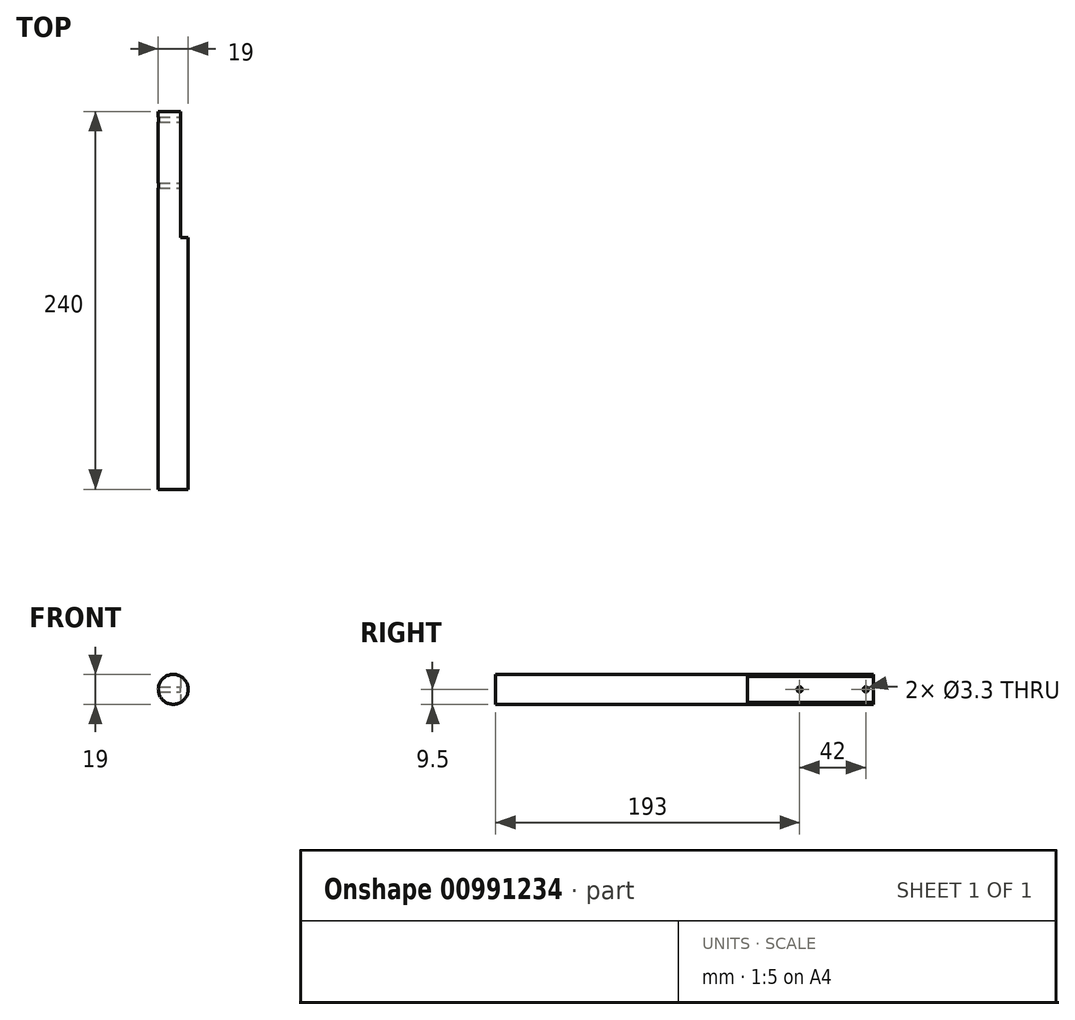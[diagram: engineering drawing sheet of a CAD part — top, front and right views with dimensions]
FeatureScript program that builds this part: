
annotation { "Feature Type Name" : "Feature", "Feature Type Description" : "" }
export const myFeature = defineFeature(function(context is Context, id is Id, definition is map)
    precondition{}
    {
        {
            var Q0;
            Q0=qCreatedBy(makeId("Front.planeOp"),FACE);
            var sketch = newSketch(context, id + "F0", { "sketchPlane" : qUnion([Q0])});
            skCircle(sketch, "E0", {"center": v(0, 0) * mm, "radius": 9.5 * mm});
            skSolve(sketch);
        }
        {
            var Q0;
            Q0 = qSketchRegion(id + "F0", true);
            extrude(context, id + "F1", {"entities" : qUnion([Q0]), "depth" : 240 * mm, "offsetDistance" : 25 * mm});
        }
        {
            var Q0;
            Q0=qCreatedBy(makeId("Right.planeOp"),FACE);
            cPlane(context, id + "F2", {"entities" : qUnion([Q0]), "cplaneType" : CPlaneType.OFFSET, "offset" : 9.5 * mm, "width" : 150 * mm, "height" : 150 * mm});
        }
        {
            var Q0;
            Q0=qCreatedBy(id+"F2.planeOp",FACE);
            var sketch = newSketch(context, id + "F3", { "sketchPlane" : qUnion([Q0])});
            skLineSegment(sketch, "E1.bottom", {"start": v(0, 22.94) * mm, "end": v(-80, 22.94) * mm});
            skLineSegment(sketch, "E1.top", {"start": v(0, -22.57) * mm, "end": v(-80, -22.57) * mm});
            skLineSegment(sketch, "E1.left", {"start": v(0, 22.94) * mm, "end": v(0, -22.57) * mm});
            skLineSegment(sketch, "E1.right", {"start": v(-80, 22.94) * mm, "end": v(-80, -22.57) * mm});
            skSolve(sketch);
        }
        {
            var Q0;
            Q0 = qSketchRegion(id + "F3", true);
            extrude(context, id + "F4", {"entities" : qUnion([Q0]), "operationType" : NewBodyOperationType.REMOVE, "oppositeDirection" : true, "depth" : 5 * mm, "offsetDistance" : 25 * mm});
        }
        {
            var Q0;
            Q0=makeQuery(id+"F4.boolean.opBoolean","COPY",FACE,{"derivedFrom":makeQuery(id+"F4.opExtrude","CAP_FACE",FACE,{"disambiguationData":[OSD([sQuery(id+"F3.wireOp",EDGE,"E1.bottom"),sQuery(id+"F3.wireOp",EDGE,"E1.top"),sQuery(id+"F3.wireOp",EDGE,"E1.left"),sQuery(id+"F3.wireOp",EDGE,"E1.right")])],"isStart":false})});
            var sketch = newSketch(context, id + "F5", { "sketchPlane" : qUnion([Q0])});
            skPoint(sketch, "E2", {"position": v(-5, 0) * mm});
            skPoint(sketch, "E3", {"position": v(-47, 0) * mm});
            skSolve(sketch);
        }
        {
            var Q0;
            Q0=sQuery(id+"F5.wireOp",VERTEX,"E3");
            var Q1;
            Q1=sQuery(id+"F5.wireOp",VERTEX,"E2");
            var Q2;
            Q2=makeQuery(id+"F1.opExtrude","SWEPT_BODY",BODY,{"disambiguationData":[OSD([sQuery(id+"F0.wireOp",EDGE,"E0")])]});
            hole(context, id + "F6", {"style" : HoleStyle.SIMPLE, "endStyle" : HoleEndStyle.THROUGH, "standardTappedOrClearance" : lookupTablePath({ "standard" : "ISO", "engagement" : "75%", "pitch" : "0.7 mm", "size" : "M4", "type" : "Tapped" }), "standardBlindInLast" : lookupTablePath({ "standard" : "ISO", "fit" : "Normal", "engagement" : "75%", "pitch" : "0.7 mm", "size" : "M4", "type" : "Clearance & tapped" }), "holeDiameter" : 3.3 * mm, "majorDiameter" : 4 * mm, "showTappedDepth" : true, "isTappedThrough" : true, "tappedDepth" : 21.25 * mm, "tapClearance" : 3, "startFromSketch" : true, "locations" : qUnion([Q0, Q1]), "scope" : qUnion([Q2])});
        }
    });
